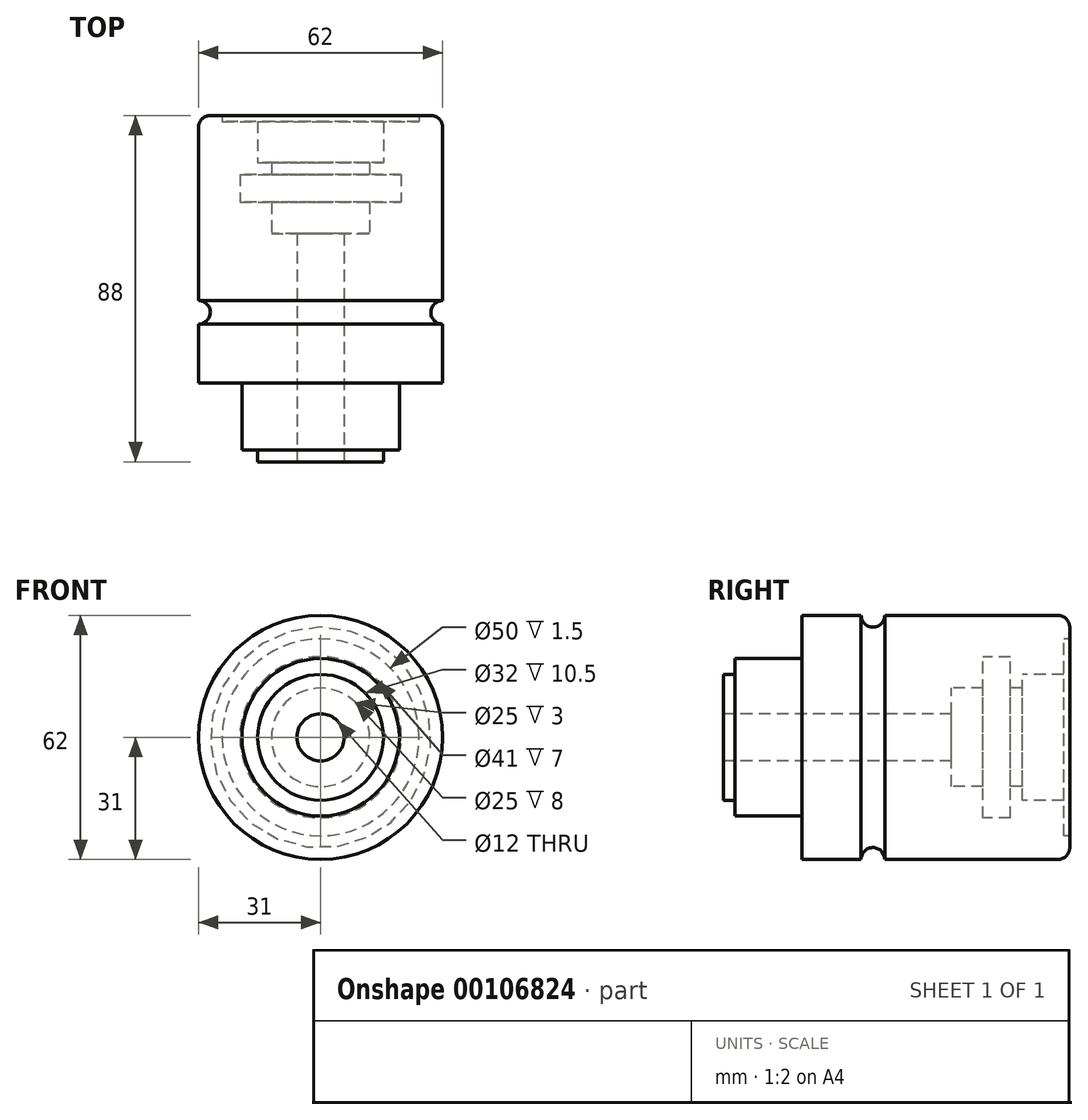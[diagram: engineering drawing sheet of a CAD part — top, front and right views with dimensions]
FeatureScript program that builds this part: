
annotation { "Feature Type Name" : "Feature", "Feature Type Description" : "" }
export const myFeature = defineFeature(function(context is Context, id is Id, definition is map)
    precondition{}
    {
        {
            var Q0;
            Q0=qCreatedBy(makeId("Right.planeOp"),FACE);
            var sketch = newSketch(context, id + "F0", { "sketchPlane" : qUnion([Q0])});
            skLineSegment(sketch, "E0", {"start": v(0, 0) * mm, "end": v(50, 0) * mm});
            skLineSegment(sketch, "E1", {"start": v(50, 0) * mm, "end": v(50, 25) * mm});
            skLineSegment(sketch, "E2", {"start": v(50, 25) * mm, "end": v(48.5, 25) * mm});
            skLineSegment(sketch, "E3", {"start": v(48.5, 25) * mm, "end": v(48.5, 16) * mm});
            skLineSegment(sketch, "E4", {"start": v(48.5, 16) * mm, "end": v(38, 16) * mm});
            skLineSegment(sketch, "E5", {"start": v(38, 16) * mm, "end": v(38, 12.5) * mm});
            skLineSegment(sketch, "E6", {"start": v(38, 12.5) * mm, "end": v(35, 12.5) * mm});
            skLineSegment(sketch, "E7", {"start": v(35, 12.5) * mm, "end": v(35, 20.5) * mm});
            skLineSegment(sketch, "E8", {"start": v(35, 20.5) * mm, "end": v(28, 20.5) * mm});
            skLineSegment(sketch, "E9", {"start": v(28, 20.5) * mm, "end": v(28, 12.5) * mm});
            skLineSegment(sketch, "E10", {"start": v(28, 12.5) * mm, "end": v(20, 12.5) * mm});
            skLineSegment(sketch, "E11", {"start": v(20, 12.5) * mm, "end": v(20, 6) * mm});
            skLineSegment(sketch, "E12", {"start": v(20, 6) * mm, "end": v(-38, 6) * mm});
            skLineSegment(sketch, "E13", {"start": v(-38, 6) * mm, "end": v(-38, 0) * mm});
            skLineSegment(sketch, "E14", {"start": v(-38, 0) * mm, "end": v(0, 0) * mm});
            skSolve(sketch);
        }
        {
            var Q0;
            Q0=qCreatedBy(makeId("Right.planeOp"),FACE);
            var sketch = newSketch(context, id + "F1", { "sketchPlane" : qUnion([Q0])});
            skLineSegment(sketch, "E15", {"start": v(-38, 0) * mm, "end": v(-38, 16) * mm});
            skLineSegment(sketch, "E16", {"start": v(-38, 16) * mm, "end": v(-35, 16) * mm});
            skLineSegment(sketch, "E17", {"start": v(-35, 16) * mm, "end": v(-35, 20) * mm});
            skLineSegment(sketch, "E18", {"start": v(-35, 20) * mm, "end": v(-18, 20) * mm});
            skLineSegment(sketch, "E19", {"start": v(-18, 20) * mm, "end": v(-18, 31) * mm});
            skLineSegment(sketch, "E20", {"start": v(-18, 31) * mm, "end": v(-3, 31) * mm});
            skLineSegment(sketch, "E21", {"start": v(0, 0) * mm, "end": v(-38, 0) * mm});
            skArc(sketch, "E22", {"start": v(-3, 31) * mm, "mid": v(0, 28) * mm, "end": v(3, 31) * mm});
            skLineSegment(sketch, "E23", {"start": v(50, 28) * mm, "end": v(50, 0) * mm});
            skLineSegment(sketch, "E24", {"start": v(50, 0) * mm, "end": v(0, 0) * mm});
            skLineSegment(sketch, "E25", {"start": v(47, 31) * mm, "end": v(3, 31) * mm});
            skPoint(sketch, "E26.visualSharp", {"position": v(50, 31) * mm});
            skArc(sketch, "E26.filletArc", {"start": v(50, 28) * mm, "mid": v(49.12, 30.12) * mm, "end": v(47, 31) * mm});
            skSolve(sketch);
        }
        {
            var Q0;
            Q0=makeQuery(id+"F1.imprint","IMPRINT",FACE,{"disambiguationData":[TD([[makeQuery(id+"F1.imprint","IMPRINT",EDGE,{"derivedFrom":sQuery(id+"F1.wireOp",EDGE,"E15")}),-1.0]])]});
            var Q1;
            Q1=sQuery(id+"F1.wireOp",EDGE,"E21");
            revolve(context, id + "F2", {"entities" : qUnion([Q0]), "axis" : qUnion([Q1]), "revolveType" : RevolveType.FULL});
        }
        {
            var Q0;
            Q0 = qSketchRegion(id + "F0", true);
            var Q1;
            Q1=sQuery(id+"F1.wireOp",EDGE,"E21");
            revolve(context, id + "F3", {"operationType" : NewBodyOperationType.REMOVE, "entities" : qUnion([Q0]), "axis" : qUnion([Q1]), "revolveType" : RevolveType.FULL, "oppositeDirection" : true});
        }
    });
